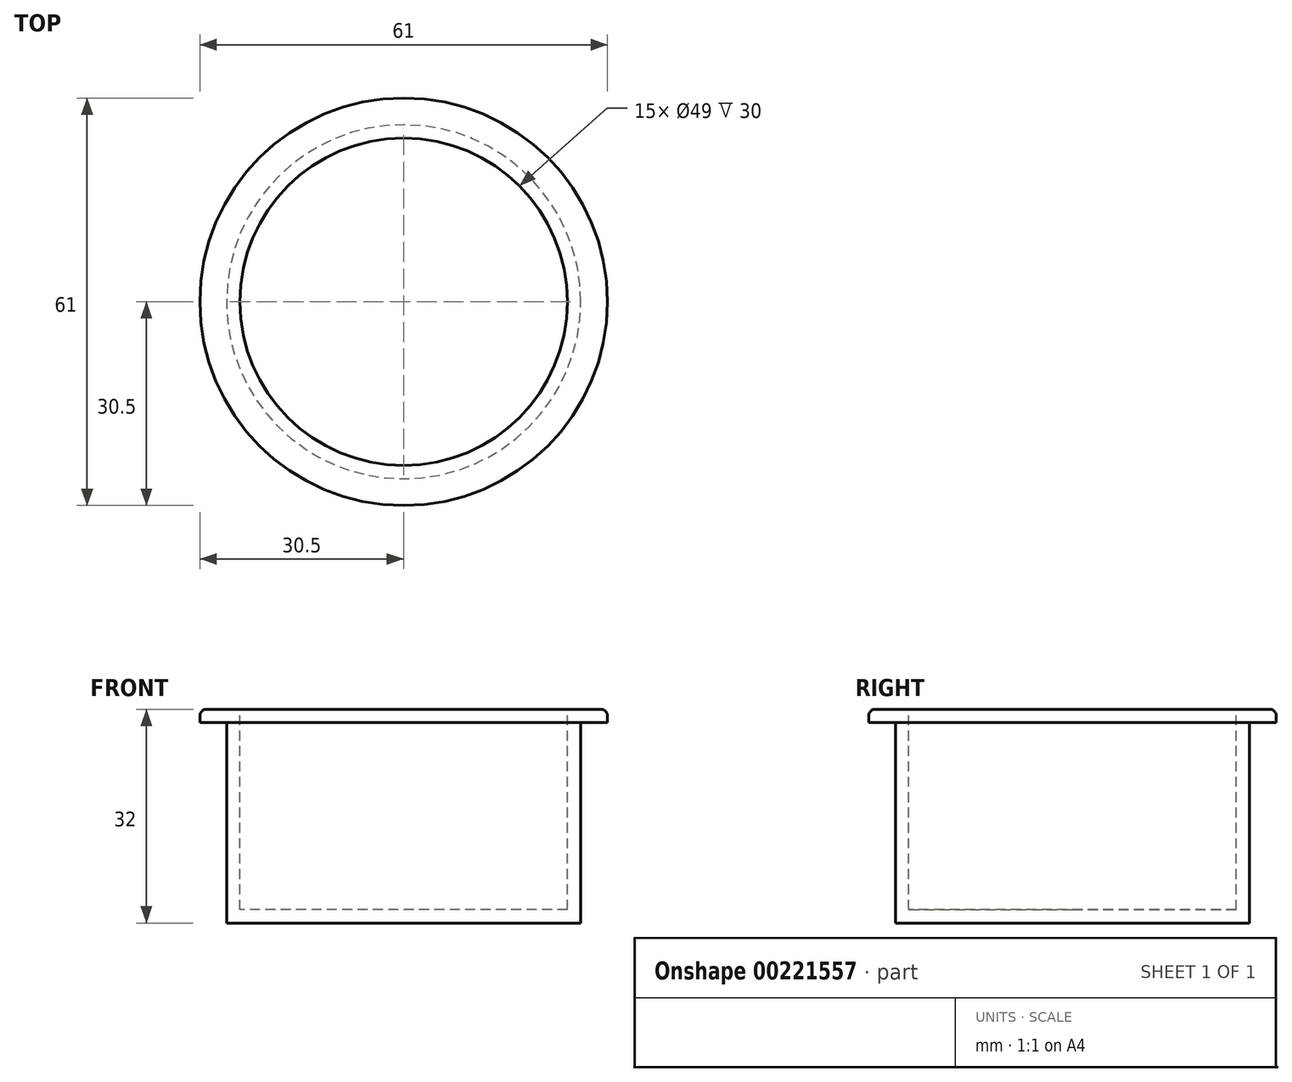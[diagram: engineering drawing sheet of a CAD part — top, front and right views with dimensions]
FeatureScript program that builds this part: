
annotation { "Feature Type Name" : "Feature", "Feature Type Description" : "" }
export const myFeature = defineFeature(function(context is Context, id is Id, definition is map)
    precondition{}
    {
        {
            var Q0;
            Q0=qCreatedBy(makeId("Front.planeOp"),FACE);
            var sketch = newSketch(context, id + "F0", { "sketchPlane" : qUnion([Q0])});
            skLineSegment(sketch, "E0", {"start": v(-24.5, -30) * mm, "end": v(0, -30) * mm});
            skLineSegment(sketch, "E1", {"start": v(-24.5, -30) * mm, "end": v(-24.5, 0) * mm});
            skLineSegment(sketch, "E2", {"start": v(-24.5, 0) * mm, "end": v(-30.5, 0) * mm});
            skLineSegment(sketch, "E3", {"start": v(-30.5, 0) * mm, "end": v(-30.5, -2) * mm});
            skLineSegment(sketch, "E4", {"start": v(-30.5, -2) * mm, "end": v(-26.5, -2) * mm});
            skLineSegment(sketch, "E5", {"start": v(-26.5, -2) * mm, "end": v(-26.5, -32) * mm});
            skLineSegment(sketch, "E6", {"start": v(-26.5, -32) * mm, "end": v(0, -32) * mm});
            skLineSegment(sketch, "E7", {"start": v(0, 5.4) * mm, "end": v(0, -58.14) * mm, "construction": true});
            skLineSegment(sketch, "E8", {"start": v(0, -30) * mm, "end": v(0, -32) * mm});
            skSolve(sketch);
        }
        {
            var Q0;
            Q0=makeQuery(id+"F0.imprint","IMPRINT",FACE,{"disambiguationData":[TD([[makeQuery(id+"F0.imprint","IMPRINT",EDGE,{"derivedFrom":sQuery(id+"F0.wireOp",EDGE,"E0")}),-1.0]])]});
            var Q1;
            Q1=sQuery(id+"F0.wireOp",EDGE,"E7");
            revolve(context, id + "F1", {"entities" : qUnion([Q0]), "axis" : qUnion([Q1]), "revolveType" : RevolveType.FULL});
        }
        {
            var Q0;
            Q0=makeQuery(id+"F1.opRevolve","SWEPT_EDGE",EDGE,{"disambiguationData":[OSD([sQuery(id+"F0.wireOp",EDGE,"E2"),sQuery(id+"F0.wireOp",EDGE,"E3")])]});
            fillet(context, id + "F2", {"entities" : qUnion([Q0]), "radius" : 1 * mm, "tangentPropagation" : true, "allowEdgeOverflow" : false});
        }
    });
